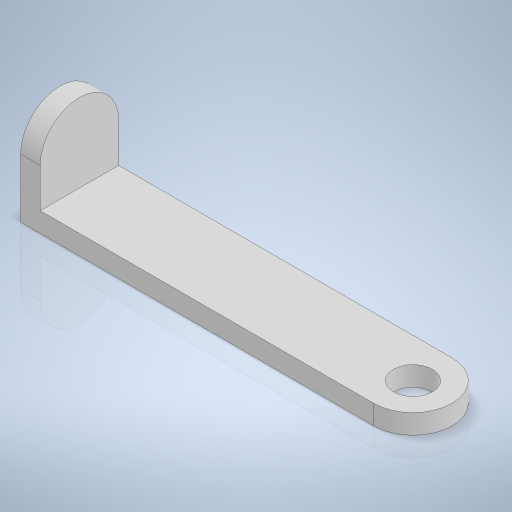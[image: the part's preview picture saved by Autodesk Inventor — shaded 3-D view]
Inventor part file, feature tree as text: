
AUTODESK INVENTOR PART (.ipt)
format: ipt  version: 2024 (Build 280153000, 153)  size: 244,224 bytes
history: native  units: mm
features: sketch x3, extrude x2, hole x1, projected_geometry x1
ambient origin geometry x8: Origin, YZ Plane, XZ Plane, XY Plane, X Axis, Y Axis, Z Axis, Center Point
bodies: Volumenkörper1 (feature_tree)
feature tree (7):
  extrude  "Extrusion1"  Depth=3.0mm
  extrude  "Extrusion2"  Depth=1.5mm
  hole  "Bohrung1"  [1 undecoded]
  sketch  "Skizze1"  dims[d0=3.0mm d1=25.5mm]
  sketch  "Skizze3"  dims[d2=1.5mm d3=0.0mm d4=7.5mm]
  projected_geometry  "Projizierte Kontur1"
  sketch  "Skizze4"  dims[d5=1.5mm d6=0.0mm d7=3.0mm d8=6.0mm d9=4.0mm d10=2.0mm d11=90.0deg d12=8.0mm d13=0.0mm]
note: 1 required parameter value undecoded (feature->parameter linkage not recoverable at this tier; creation-order binding heuristic only, values carry confidence <= 0.55)
